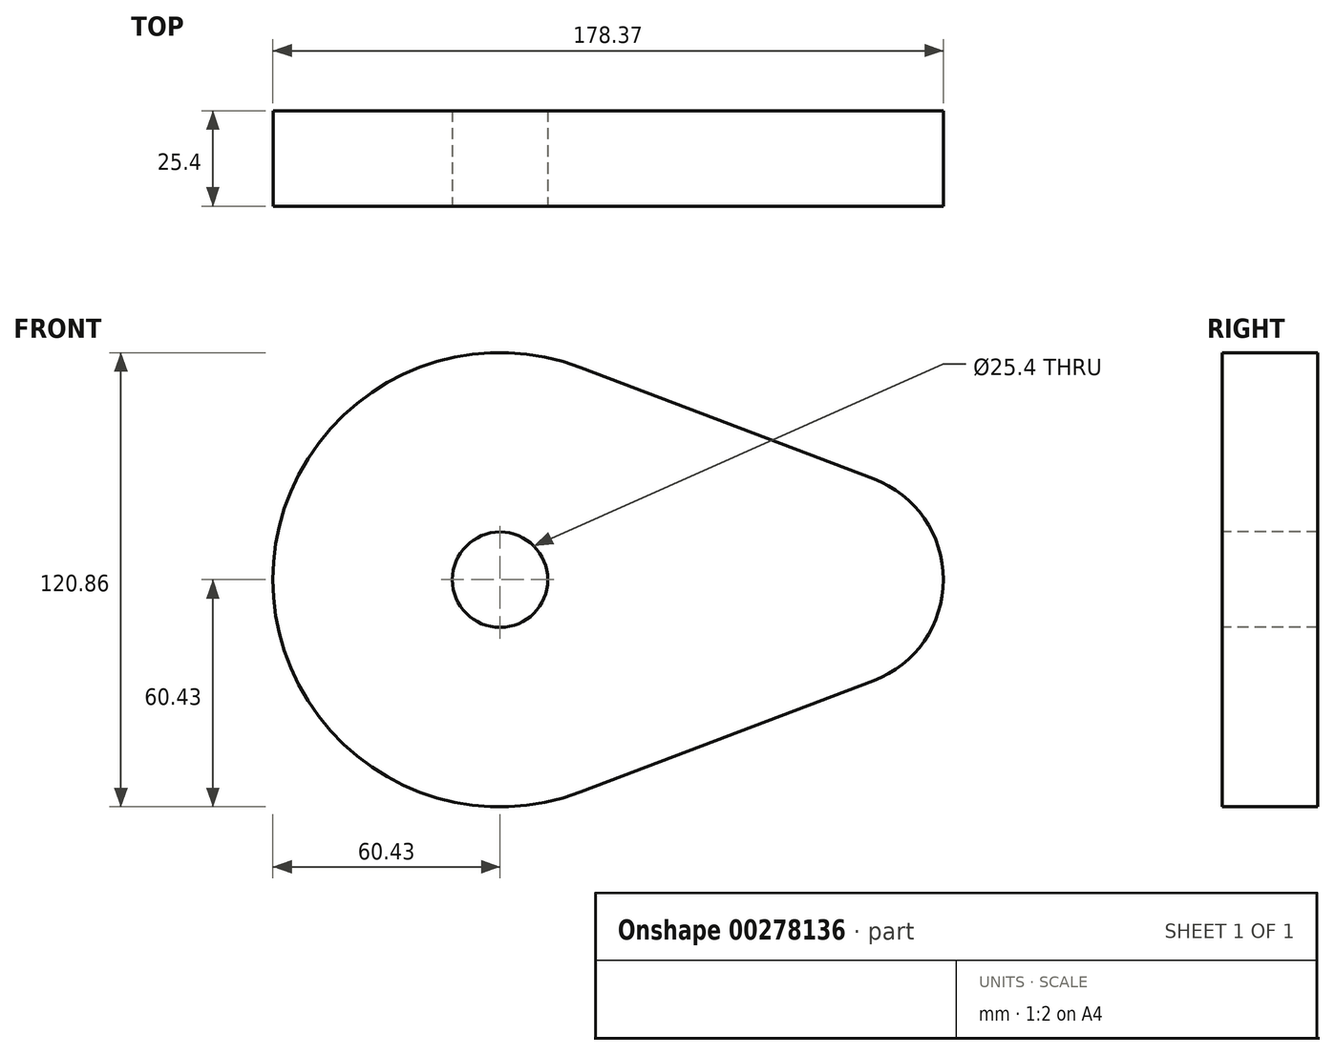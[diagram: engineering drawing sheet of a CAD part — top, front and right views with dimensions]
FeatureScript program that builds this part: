
annotation { "Feature Type Name" : "Feature", "Feature Type Description" : "" }
export const myFeature = defineFeature(function(context is Context, id is Id, definition is map)
    precondition{}
    {
        {
            var Q0;
            Q0=qCreatedBy(makeId("Front.planeOp"),FACE);
            var sketch = newSketch(context, id + "F0", { "sketchPlane" : qUnion([Q0])});
            skCircle(sketch, "E0", {"center": v(0, 0) * mm, "radius": 60.43 * mm});
            skLineSegment(sketch, "E1", {"start": v(21.46, 56.49) * mm, "end": v(99.4, 26.88) * mm});
            skLineSegment(sketch, "E2", {"start": v(0, 0) * mm, "end": v(89.18, 0) * mm, "construction": true});
            skLineSegment(sketch, "E3.MirrorCS", {"start": v(21.46, -56.49) * mm, "end": v(99.4, -26.88) * mm});
            skCircle(sketch, "E4", {"center": v(89.18, 0) * mm, "radius": 28.76 * mm});
            skSolve(sketch);
        }
        {
            var Q0;
            {var subQ0=sQuery(id+"F0.wireOp",EDGE,"E0");var subQ1=makeQuery(id+"F0.imprint","INTERSECT",VERTEX,{"derivedFrom":[subQ0,sQuery(id+"F0.wireOp",EDGE,"E1")]});Q0=makeQuery(id+"F0.imprint","IMPRINT",FACE,{"disambiguationData":[TD([[makeQuery(id+"F0.imprint","IMPRINT",EDGE,{"disambiguationData":[TD([[subQ1,1.0]])],"derivedFrom":subQ0}),1.0]])]});}
            var Q1;
            {var subQ0=sQuery(id+"F0.wireOp",EDGE,"E1");Q1=makeQuery(id+"F0.imprint","IMPRINT",FACE,{"disambiguationData":[TD([[makeQuery(id+"F0.imprint","IMPRINT",EDGE,{"derivedFrom":subQ0}),-1.0]])]});}
            var Q2;
            {var subQ0=sQuery(id+"F0.wireOp",EDGE,"E3.MirrorCS");Q2=makeQuery(id+"F0.imprint","IMPRINT",FACE,{"disambiguationData":[TD([[makeQuery(id+"F0.imprint","IMPRINT",EDGE,{"derivedFrom":subQ0}),1.0]])]});}
            var Q3;
            {var subQ0=sQuery(id+"F0.wireOp",EDGE,"E4");var subQ1=makeQuery(id+"F0.imprint","INTERSECT",VERTEX,{"derivedFrom":[sQuery(id+"F0.wireOp",EDGE,"E1"),subQ0]});Q3=makeQuery(id+"F0.imprint","IMPRINT",FACE,{"disambiguationData":[TD([[makeQuery(id+"F0.imprint","IMPRINT",EDGE,{"disambiguationData":[TD([[subQ1,-1.0]])],"derivedFrom":subQ0}),1.0]])]});}
            extrude(context, id + "F1", {"entities" : qUnion([Q0, Q1, Q2, Q3]), "depth" : 25.4 * mm});
        }
        {
            var Q0;
            Q0=makeQuery(id+"F1.opExtrude","CAP_FACE",FACE,{"disambiguationData":[OSD([sQuery(id+"F0.wireOp",EDGE,"E0"),sQuery(id+"F0.wireOp",EDGE,"E1"),sQuery(id+"F0.wireOp",EDGE,"E3.MirrorCS"),sQuery(id+"F0.wireOp",EDGE,"E4")])],"isStart":false});
            var sketch = newSketch(context, id + "F2", { "sketchPlane" : qUnion([Q0])});
            skCircle(sketch, "E5", {"center": v(0, 0) * mm, "radius": 12.7 * mm});
            skSolve(sketch);
        }
        {
            var Q0;
            Q0=makeQuery(id+"F2.imprint","IMPRINT",FACE,{"disambiguationData":[TD([[makeQuery(id+"F2.imprint","IMPRINT",EDGE,{"derivedFrom":sQuery(id+"F2.wireOp",EDGE,"E5")}),1.0]])]});
            extrude(context, id + "F3", {"entities" : qUnion([Q0]), "operationType" : NewBodyOperationType.REMOVE, "endBound" : BoundingType.THROUGH_ALL, "oppositeDirection" : true, "depth" : 25.4 * mm});
        }
    });
